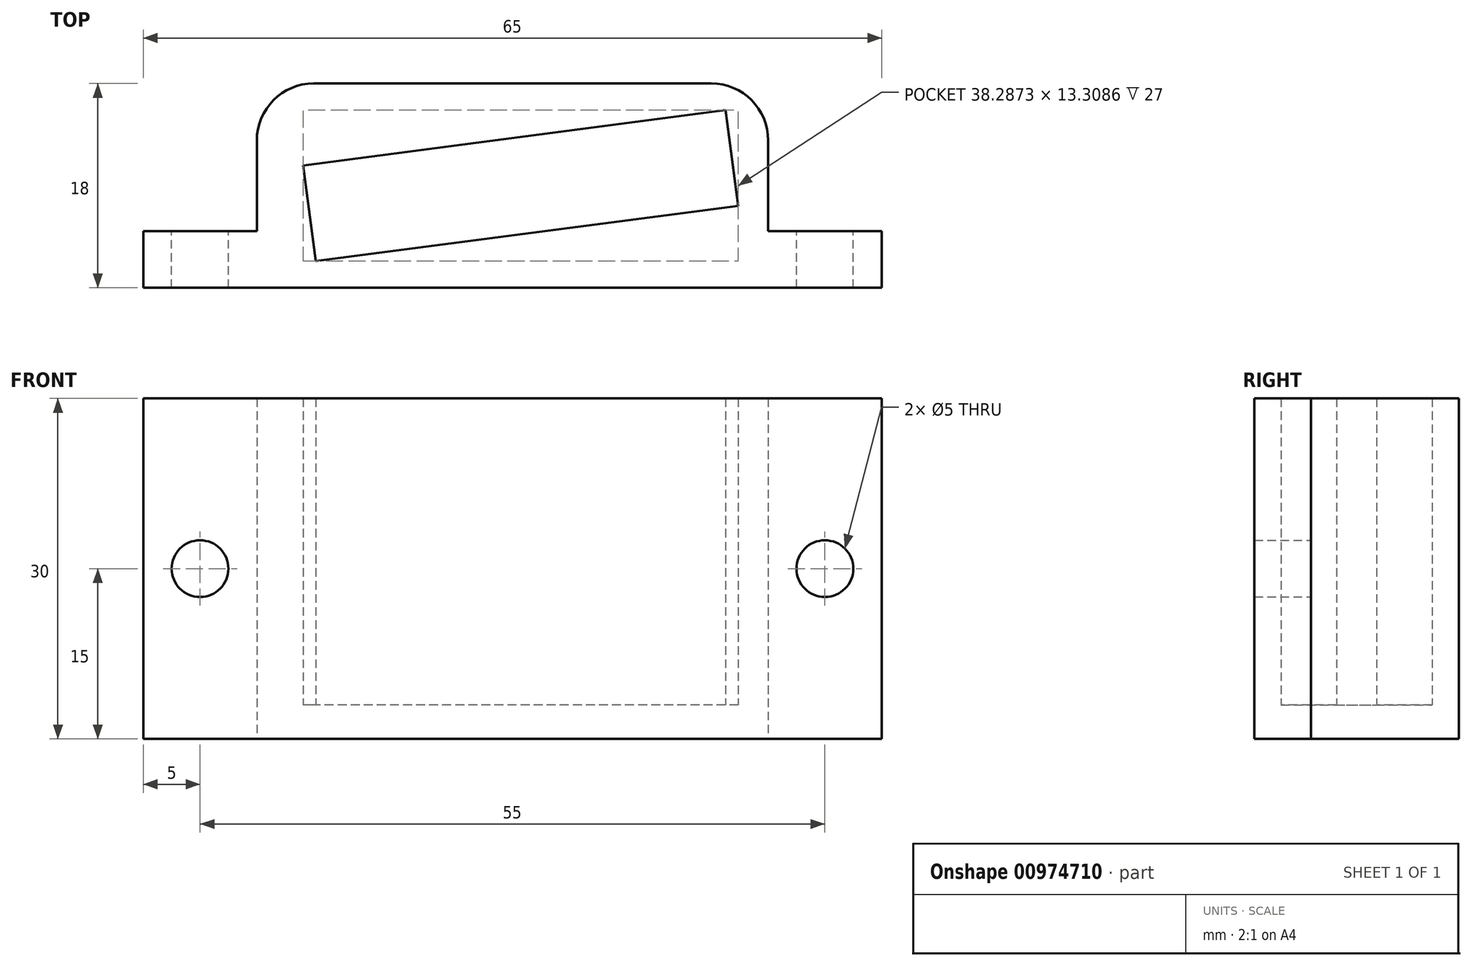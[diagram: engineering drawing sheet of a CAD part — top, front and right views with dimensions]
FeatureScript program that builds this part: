
annotation { "Feature Type Name" : "Feature", "Feature Type Description" : "" }
export const myFeature = defineFeature(function(context is Context, id is Id, definition is map)
    precondition{}
    {
        {
            var Q0;
            Q0=qCreatedBy(makeId("Top.planeOp"),FACE);
            var sketch = newSketch(context, id + "F0", { "sketchPlane" : qUnion([Q0])});
            skLineSegment(sketch, "E0.bottom", {"start": v(32.5, -9) * mm, "end": v(-32.5, -9) * mm});
            skLineSegment(sketch, "E0.top", {"start": v(22.5, 9) * mm, "end": v(-22.5, 9) * mm});
            skLineSegment(sketch, "E0.left", {"start": v(32.5, -9) * mm, "end": v(32.5, -4) * mm});
            skLineSegment(sketch, "E0.right", {"start": v(-32.5, -9) * mm, "end": v(-32.5, -4) * mm});
            skPoint(sketch, "E0.middle", {"position": v(0, 0) * mm});
            skLineSegment(sketch, "E1.bottom", {"start": v(19.86, -1.78) * mm, "end": v(-17.32, -6.66) * mm});
            skLineSegment(sketch, "E1.top", {"start": v(18.76, 6.65) * mm, "end": v(-18.42, 1.77) * mm});
            skLineSegment(sketch, "E1.left", {"start": v(19.86, -1.78) * mm, "end": v(18.76, 6.65) * mm});
            skLineSegment(sketch, "E1.right", {"start": v(-17.32, -6.66) * mm, "end": v(-18.42, 1.77) * mm});
            skLineSegment(sketch, "E2", {"start": v(0, 0) * mm, "end": v(-14.43, 0) * mm, "construction": true});
            skLineSegment(sketch, "E3", {"start": v(32.5, -4) * mm, "end": v(22.5, -4) * mm});
            skLineSegment(sketch, "E4", {"start": v(22.5, -4) * mm, "end": v(22.5, 9) * mm});
            skLineSegment(sketch, "E5", {"start": v(-32.5, -4) * mm, "end": v(-22.5, -4) * mm});
            skLineSegment(sketch, "E6", {"start": v(-22.5, -4) * mm, "end": v(-22.5, 9) * mm});
            skPoint(sketch, "E7.orphan", {"position": v(-32.5, 9) * mm});
            skPoint(sketch, "E8.orphan", {"position": v(32.5, 9) * mm});
            skSolve(sketch);
        }
        {
            var Q0;
            Q0=makeQuery(id+"F0.imprint","IMPRINT",FACE,{"disambiguationData":[TD([[makeQuery(id+"F0.imprint","IMPRINT",EDGE,{"derivedFrom":sQuery(id+"F0.wireOp",EDGE,"E0.bottom")}),-1.0]])]});
            extrude(context, id + "F1", {"entities" : qUnion([Q0]), "depth" : 30 * mm, "offsetDistance" : 25 * mm});
        }
        {
            var Q0;
            Q0=makeQuery(id+"F0.imprint","IMPRINT",FACE,{"disambiguationData":[TD([[makeQuery(id+"F0.imprint","IMPRINT",EDGE,{"derivedFrom":sQuery(id+"F0.wireOp",EDGE,"E1.bottom")}),-1.0]])]});
            extrude(context, id + "F2", {"entities" : qUnion([Q0]), "operationType" : NewBodyOperationType.ADD, "depth" : 3 * mm, "offsetDistance" : 25 * mm});
        }
        {
            var Q0;
            Q0=makeQuery(id+"F1.opExtrude","SWEPT_EDGE",EDGE,{"disambiguationData":[OSD([sQuery(id+"F0.wireOp",EDGE,"E0.top"),sQuery(id+"F0.wireOp",EDGE,"E4")])]});
            var Q1;
            Q1=makeQuery(id+"F1.opExtrude","SWEPT_EDGE",EDGE,{"disambiguationData":[OSD([sQuery(id+"F0.wireOp",EDGE,"E0.top"),sQuery(id+"F0.wireOp",EDGE,"E6")])]});
            fillet(context, id + "F3", {"entities" : qUnion([Q0, Q1]), "radius" : 5 * mm, "tangentPropagation" : true, "allowEdgeOverflow" : false});
        }
        {
            var Q0;
            Q0=makeQuery(id+"F1.opExtrude","SWEPT_FACE",FACE,{"disambiguationData":[OSD([sQuery(id+"F0.wireOp",EDGE,"E3")])]});
            var sketch = newSketch(context, id + "F4", { "sketchPlane" : qUnion([Q0])});
            skLineSegment(sketch, "E9", {"start": v(-27.5, 0) * mm, "end": v(-27.5, 30) * mm, "construction": true});
            skCircle(sketch, "E10", {"center": v(-27.5, 15) * mm, "radius": 2.5 * mm});
            skSolve(sketch);
        }
        {
            var Q0;
            Q0=makeQuery(id+"F1.opExtrude","SWEPT_FACE",FACE,{"disambiguationData":[OSD([sQuery(id+"F0.wireOp",EDGE,"E5")])]});
            var sketch = newSketch(context, id + "F5", { "sketchPlane" : qUnion([Q0])});
            skLineSegment(sketch, "E11", {"start": v(27.5, 0) * mm, "end": v(27.5, 30) * mm, "construction": true});
            skCircle(sketch, "E12", {"center": v(27.5, 15) * mm, "radius": 2.5 * mm});
            skSolve(sketch);
        }
        {
            var Q0;
            Q0=makeQuery(id+"F5.imprint","IMPRINT",FACE,{"disambiguationData":[TD([[makeQuery(id+"F5.imprint","IMPRINT",EDGE,{"derivedFrom":sQuery(id+"F5.wireOp",EDGE,"E12")}),1.0]])]});
            var Q1;
            Q1=makeQuery(id+"F4.imprint","IMPRINT",FACE,{"disambiguationData":[TD([[makeQuery(id+"F4.imprint","IMPRINT",EDGE,{"derivedFrom":sQuery(id+"F4.wireOp",EDGE,"E10")}),1.0]])]});
            extrude(context, id + "F6", {"entities" : qUnion([Q0, Q1]), "operationType" : NewBodyOperationType.REMOVE, "oppositeDirection" : true, "depth" : 25 * mm, "offsetDistance" : 25 * mm});
        }
    });
